# Revit family: Legrand Eclairage de Séurité_Bloc a Phare-SPOTLIGHT
name_source: partatom
category: Luminaires
units: mm (PartAtom-declared; Revit-internal decimal feet)

## family parameters
Cote de connecteur circulaire = Utiliser le diamètre
Couper avec des vides une fois chargée = Non
Hôte = Face
Partagée = Non
Repere pour localisation dans la piece = Non
Source d'éclairage = Non
Type d'élément = Normal

## types (8) — shared parameters
Alimentation de secours = Autonome (batterie individuelle)
Classe ETIM = EC001957-Luminaire d'éclairage de sécurité
Classe de protection = II
Conditions Générale d'Utilisation = https://export.legrand.com
Consommation en veille = 0 A
Couleur = Noir
Elévation par défaut = 2300 mm
Fabricant = Legrand
Fonction = Éclairage d'évacuation et d'ambiance
Fréquence = 50/60 Hz
Hauteur = 94 mm
IK = 07
IP = 65
Matière = Plastique
Mode de pose = Montage en saillie (mur)
Objet Connecté = Non
Puissance du système = 1 W
Temperature d'utilisation MIN-MAX = 0°C +35°C
Tension = 230 VAC
Type de commutation = Non permanent
Type de connexion = autre
Type de pictogramme = autre
URL = https://www.legrand.fr
capacité des bornes = 1,5-2,5 mm2
source lumineuse = LED non interchangeable
état des accus = Lithium-ion

## per-type parameters (varying)
| type | 1 phare 1000lm | 2 phares 1500lm | 2 phares 2500lm | Adressable | Autonomie | Batterie de rechange | Code EAN | Description Produit | Flux lumineux utile | Large | Largeur | Long | Longueur | Référence / Modèle | Système de contrôle |
| Spotlight Autotest 2500 lm 1H | Non | Non | Oui | Non | 1 H | 2 x 660977 | 3414972656030 | BAP AVEC 2 PHARES A LEDS NON PERMANENT 2500LM 1H AUTOTEST | 2500 lm | 240 mm  [stored 0.787402 ft] | 240 mm  [stored 0.787402 ft] | 286 mm | 286 mm | 660463 | Auto-test automatique |
| Spotlight Autotest 1000 lm 1H | Oui | Non | Non | Non | 1 H | 660976 | 3414972656016 | BAP AVEC 1 PHARE A LEDS NON PERMANENT 1000LM 1H AUTOTEST | 1000 lm | 137 mm  [stored 0.449475 ft] | 137 mm  [stored 0.449475 ft] | 409 mm | 409 mm | 660460 | Auto-test automatique |
| Spotlight Autotest 1500 lm 1H | Non | Oui | Non | Non | 1 H | 1 x 660977 | 3414972656023 | BAP AVEC 2 PHARES A LEDS NON PERMANENT 1500LM 1H AUTOTEST | 1500 lm | 240 mm  [stored 0.787402 ft] | 240 mm  [stored 0.787402 ft] | 286 mm | 286 mm | 660462 | Auto-test automatique |
| Spotlight Autotest 1500 lm 2H | Non | Oui | Non | Non | 2 H | 2 x 660977 | 3414972656047 | BAP AVEC 2 PHARES A LEDS NON PERMANENT 1500LM 2H AUTOTEST | 1500 lm | 240 mm  [stored 0.787402 ft] | 240 mm  [stored 0.787402 ft] | 286 mm | 286 mm | 660465 | Auto-test automatique |
| Spotlight Standard 1000 lm 1H | Oui | Non | Non | Non | 1 H | 660976 | 3414972656054 | BAP AVEC 1 PHARE A LEDS NON PERMANENT 1000LM 1H STANDARD | 1000 lm | 137 mm  [stored 0.449475 ft] | 137 mm  [stored 0.449475 ft] | 409 mm | 409 mm | 661460 | Touche de contrôle |
| Spotlight Standard 1500 lm 1H | Non | Oui | Non | Non | 1 H | 660977 | 3414972656061 | BAP AVEC 2 PHARES A LEDS NON PERMANENT 1500LM 1H STANDARD | 1500 lm | 240 mm  [stored 0.787402 ft] | 240 mm  [stored 0.787402 ft] | 286 mm | 286 mm | 661462 | Touche de contrôle |
| Spotlight Standard 2500 lm 1H | Non | Non | Oui | Non | 1 H | 2 x 660977 | 3414972656078 | BAP AVEC 2 PHARES A LEDS NON PERMANENT 2500LM 1H STANDARD | 2500 lm | 240 mm  [stored 0.787402 ft] | 240 mm  [stored 0.787402 ft] | 286 mm | 286 mm | 661463 | Touche de contrôle |
| Spotlight Adressable 2500 lm 1H | Non | Non | Oui | Oui | 1 H | 2 x 660977 | 3414972656085 | BAP AVEC 2 PHARES A LEDS NON PERMANENT 2500LM 1H ADRESSABLE | 2500 lm | 240 mm  [stored 0.787402 ft] | 240 mm  [stored 0.787402 ft] | 286 mm | 286 mm | 662463 | Auto-test automatique |

note: [stored X ft] marks values corroborated as IEEE doubles in the binary element streams (Revit-internal decimal feet)
